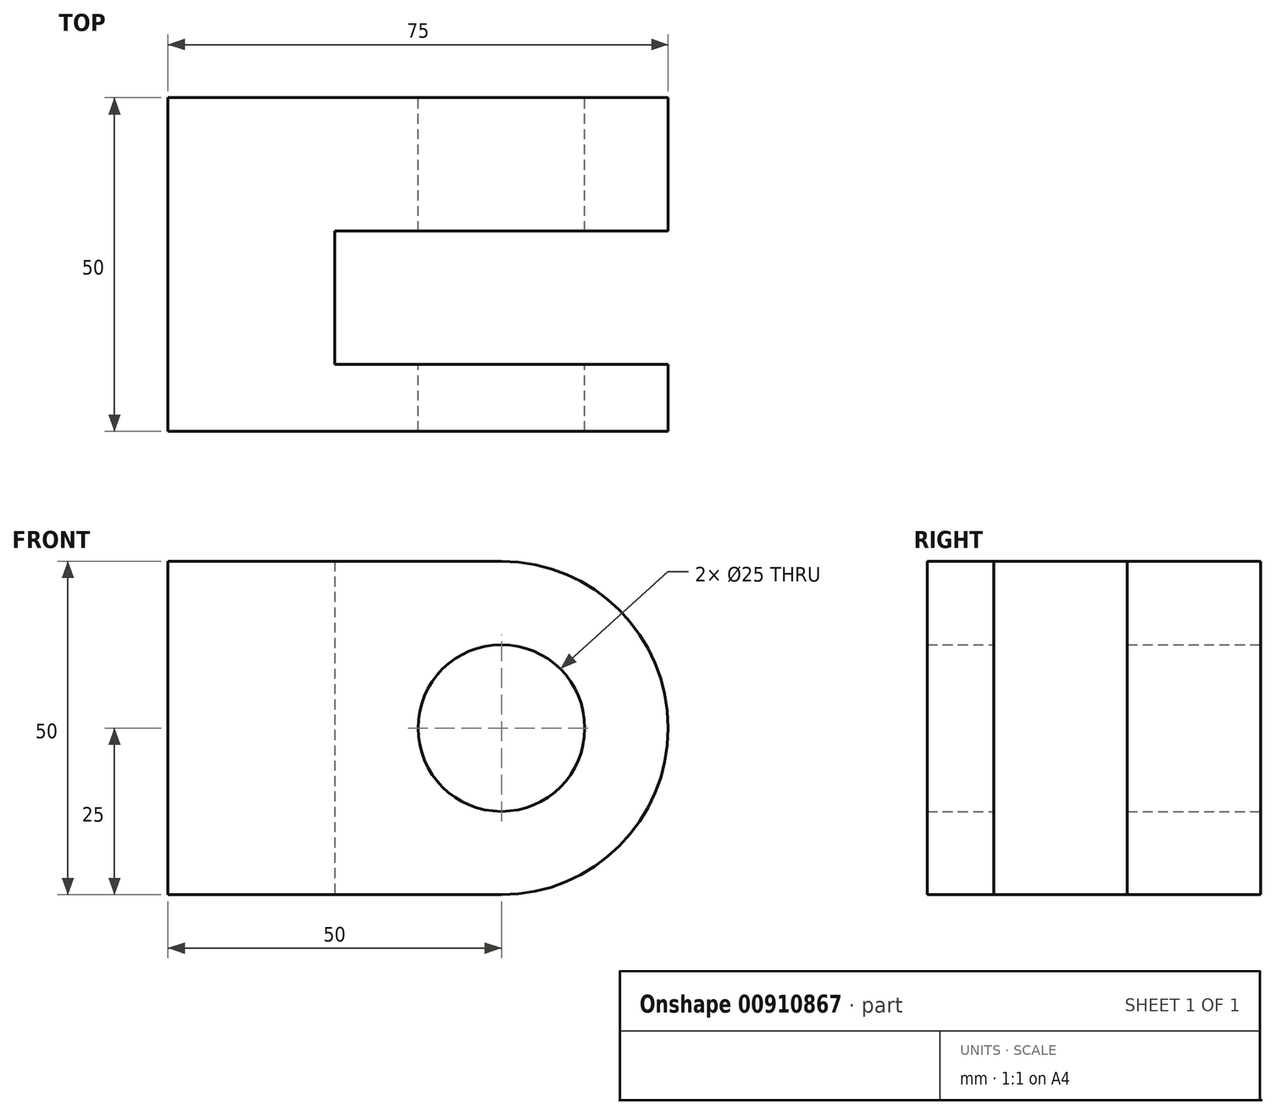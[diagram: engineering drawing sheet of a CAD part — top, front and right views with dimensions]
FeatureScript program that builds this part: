
annotation { "Feature Type Name" : "Feature", "Feature Type Description" : "" }
export const myFeature = defineFeature(function(context is Context, id is Id, definition is map)
    precondition{}
    {
        {
            var Q0;
            Q0=qCreatedBy(makeId("Front.planeOp"),FACE);
            var sketch = newSketch(context, id + "F0", { "sketchPlane" : qUnion([Q0])});
            skCircle(sketch, "E0", {"center": v(0, 0) * mm, "radius": 12.5 * mm});
            skArc(sketch, "E1", {"start": v(0, -25) * mm, "mid": v(25, 0) * mm, "end": v(0, 25) * mm});
            skLineSegment(sketch, "E2", {"start": v(0, 25) * mm, "end": v(-50, 25) * mm});
            skLineSegment(sketch, "E3", {"start": v(-50, 25) * mm, "end": v(-50, -25) * mm});
            skLineSegment(sketch, "E4", {"start": v(-50, -25) * mm, "end": v(0, -25) * mm});
            skSolve(sketch);
        }
        {
            var Q0;
            Q0 = qSketchRegion(id + "F0", true);
            extrude(context, id + "F1", {"entities" : qUnion([Q0]), "depth" : 20 * mm, "offsetDistance" : 25 * mm});
        }
        {
            var Q0;
            Q0=makeQuery(id+"F1.opExtrude","CAP_FACE",FACE,{"disambiguationData":[OSD([sQuery(id+"F0.wireOp",EDGE,"E0"),sQuery(id+"F0.wireOp",EDGE,"E1"),sQuery(id+"F0.wireOp",EDGE,"E2"),sQuery(id+"F0.wireOp",EDGE,"E3"),sQuery(id+"F0.wireOp",EDGE,"E4")])],"isStart":false});
            cPlane(context, id + "F2", {"entities" : qUnion([Q0]), "cplaneType" : CPlaneType.OFFSET, "offset" : 20 * mm, "width" : 150 * mm, "height" : 150 * mm});
        }
        {
            var Q0;
            Q0=qCreatedBy(id+"F2.planeOp",FACE);
            var sketch = newSketch(context, id + "F3", { "sketchPlane" : qUnion([Q0])});
            skLineSegment(sketch, "E5.0.0", {"start": v(-50, 25) * mm, "end": v(-50, -25) * mm});
            skLineSegment(sketch, "E5.0.1", {"start": v(-50, -25) * mm, "end": v(0, -25) * mm});
            skArc(sketch, "E5.0.2", {"start": v(0, -25) * mm, "mid": v(25, 0) * mm, "end": v(0, 25) * mm});
            skLineSegment(sketch, "E5.0.3", {"start": v(0, 25) * mm, "end": v(-50, 25) * mm});
            skCircle(sketch, "E6.0", {"center": v(0, 0) * mm, "radius": 12.5 * mm});
            skSolve(sketch);
        }
        {
            var Q0;
            Q0=makeQuery(id+"F3.imprint","IMPRINT",FACE,{"disambiguationData":[TD([[makeQuery(id+"F3.imprint","IMPRINT",EDGE,{"derivedFrom":sQuery(id+"F3.wireOp",EDGE,"E5.0.0")}),1.0]])]});
            extrude(context, id + "F4", {"entities" : qUnion([Q0]), "depth" : 10 * mm, "offsetDistance" : 25 * mm});
        }
        {
            var Q0;
            Q0=makeQuery(id+"F1.opExtrude","CAP_FACE",FACE,{"disambiguationData":[OSD([sQuery(id+"F0.wireOp",EDGE,"E0"),sQuery(id+"F0.wireOp",EDGE,"E1"),sQuery(id+"F0.wireOp",EDGE,"E2"),sQuery(id+"F0.wireOp",EDGE,"E3"),sQuery(id+"F0.wireOp",EDGE,"E4")])],"isStart":false});
            var sketch = newSketch(context, id + "F5", { "sketchPlane" : qUnion([Q0])});
            skLineSegment(sketch, "E7.bottom", {"start": v(-50, 25) * mm, "end": v(-25, 25) * mm});
            skLineSegment(sketch, "E7.top", {"start": v(-50, -25) * mm, "end": v(-25, -25) * mm});
            skLineSegment(sketch, "E7.left", {"start": v(-50, 25) * mm, "end": v(-50, -25) * mm});
            skLineSegment(sketch, "E7.right", {"start": v(-25, 25) * mm, "end": v(-25, -25) * mm});
            skSolve(sketch);
        }
        {
            var Q0;
            Q0=makeQuery(id+"F5.imprint","IMPRINT",FACE,{"disambiguationData":[TD([[makeQuery(id+"F5.imprint","IMPRINT",EDGE,{"derivedFrom":sQuery(id+"F5.wireOp",EDGE,"E7.bottom")}),1.0]])]});
            extrude(context, id + "F6", {"entities" : qUnion([Q0]), "operationType" : NewBodyOperationType.ADD, "endBound" : BoundingType.UP_TO_NEXT, "depth" : 25 * mm, "offsetDistance" : 25 * mm});
        }
    });
